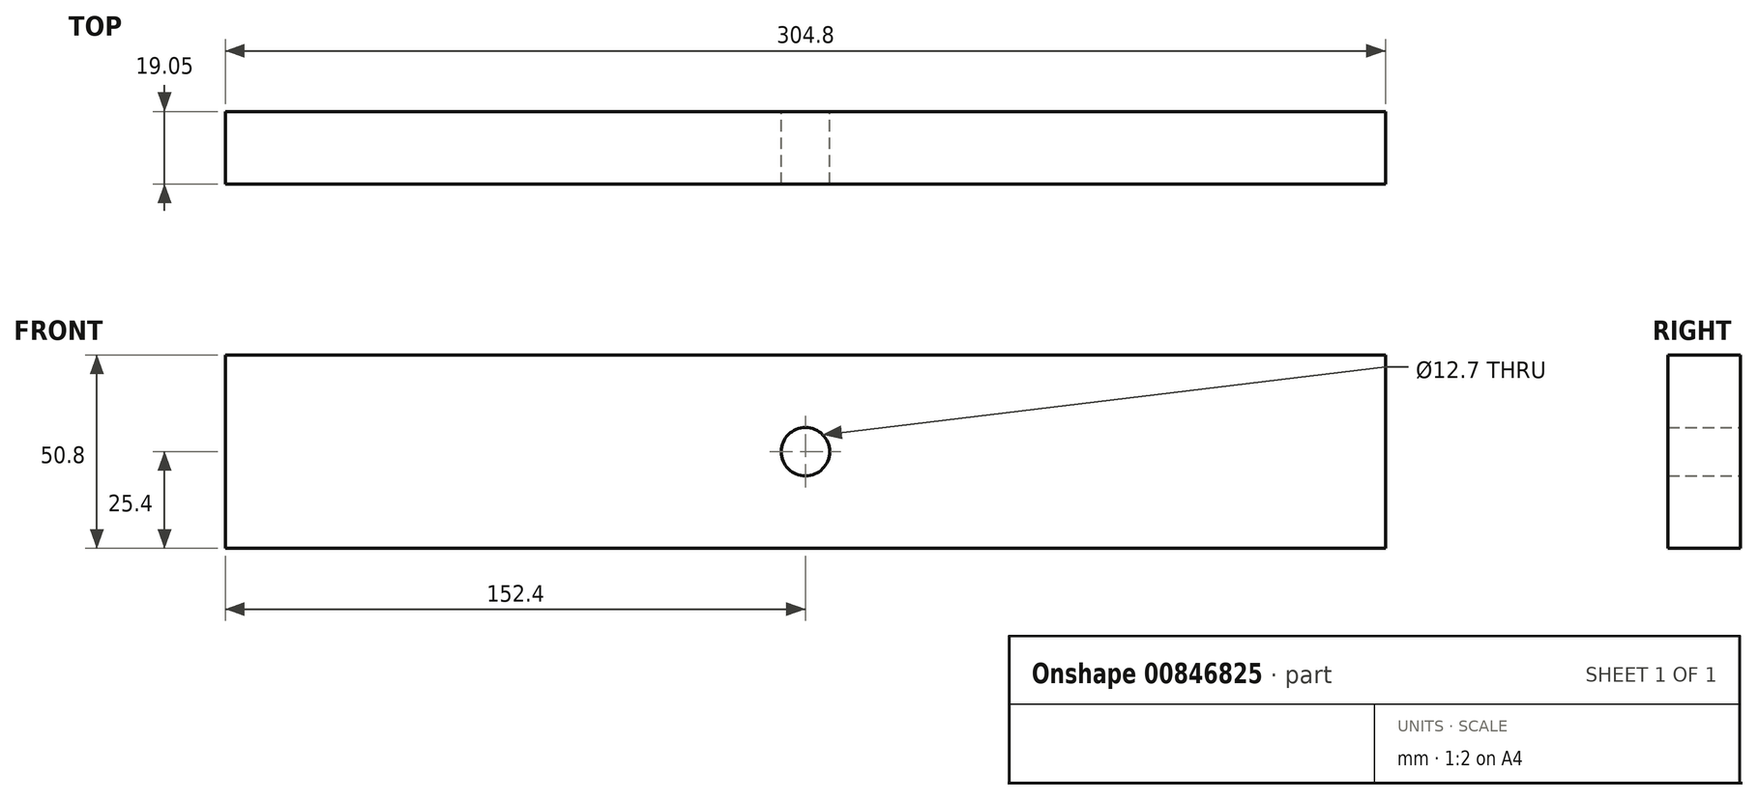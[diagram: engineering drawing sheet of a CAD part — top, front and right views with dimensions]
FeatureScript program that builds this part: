
annotation { "Feature Type Name" : "Feature", "Feature Type Description" : "" }
export const myFeature = defineFeature(function(context is Context, id is Id, definition is map)
    precondition{}
    {
        {
            var Q0;
            Q0=qCreatedBy(makeId("Front.planeOp"), FACE);
            var sketch = newSketch(context, id + "F0", { "sketchPlane" : qUnion([Q0])});
            skLineSegment(sketch, "E0.bottom", {"start": v(-152.4, 25.4) * mm, "end": v(152.4, 25.4) * mm});
            skLineSegment(sketch, "E0.top", {"start": v(-152.4, -25.4) * mm, "end": v(152.4, -25.4) * mm});
            skLineSegment(sketch, "E0.left", {"start": v(-152.4, 25.4) * mm, "end": v(-152.4, -25.4) * mm});
            skLineSegment(sketch, "E0.right", {"start": v(152.4, 25.4) * mm, "end": v(152.4, -25.4) * mm});
            skLineSegment(sketch, "E1", {"start": v(-152.4, -25.4) * mm, "end": v(152.4, 25.4) * mm, "construction": true});
            skCircle(sketch, "E2", {"center": v(0, 0) * mm, "radius": 6.35 * mm});
            skSolve(sketch);
        }
        {
            var Q0;
            Q0 = qSketchRegion(id + "F0", true);
            extrude(context, id + "F1", {"entities" : qUnion([Q0]), "flatOperationType" : FlatOperationType.REMOVE, "depth" : 19.05 * mm, "offsetDistance" : 25.4 * mm, "domain" : OperationDomain.MODEL});
        }
    });
